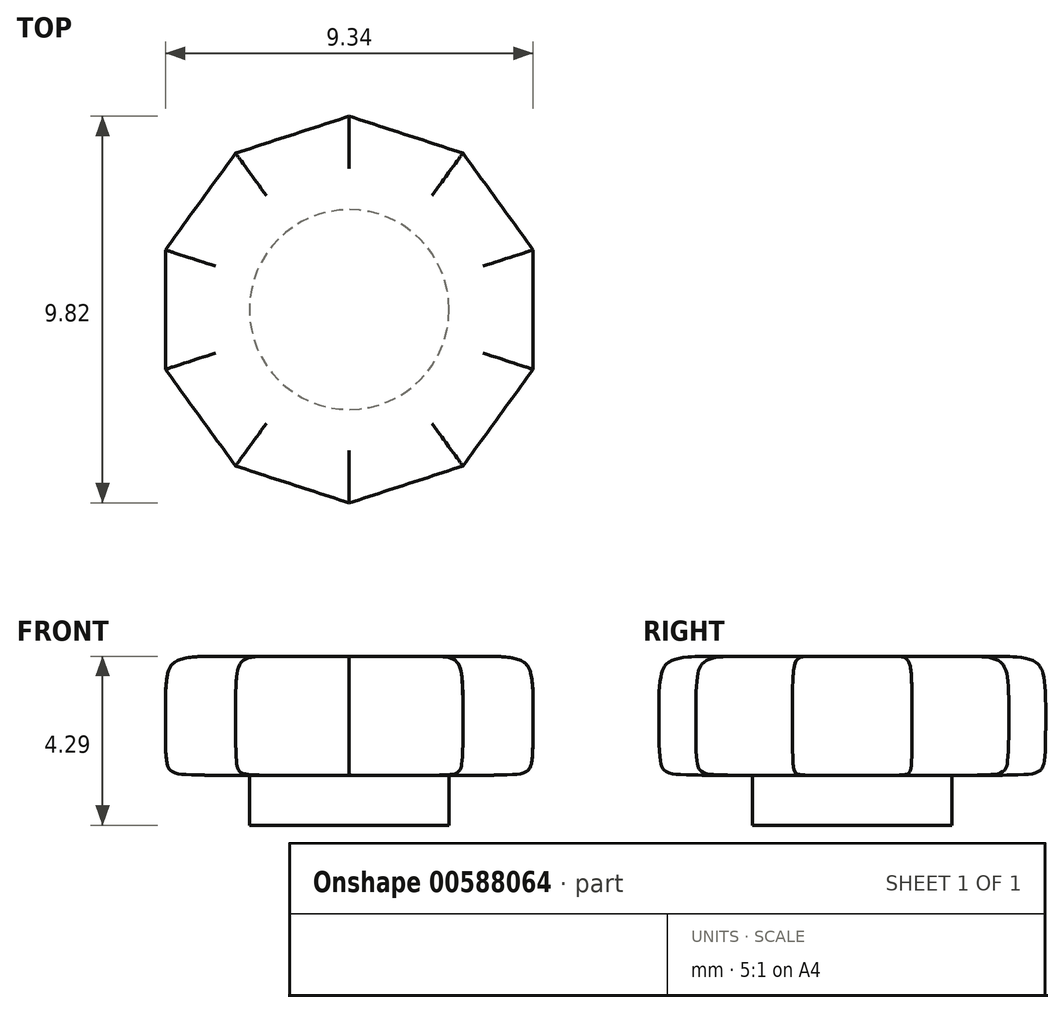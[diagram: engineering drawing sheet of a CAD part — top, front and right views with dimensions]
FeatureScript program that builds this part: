
annotation { "Feature Type Name" : "Feature", "Feature Type Description" : "" }
export const myFeature = defineFeature(function(context is Context, id is Id, definition is map)
    precondition{}
    {
        {
            var Q0;
            Q0=qCreatedBy(makeId("Top.planeOp"),FACE);
            var sketch = newSketch(context, id + "F0", { "sketchPlane" : qUnion([Q0])});
            skCircle(sketch, "E0.cCircle", {"center": v(0, 0) * mm, "radius": 4.67 * mm, "construction": true});
            skLineSegment(sketch, "E0.0", {"start": v(4.67, 1.52) * mm, "end": v(4.67, -1.52) * mm});
            skLineSegment(sketch, "E0.1", {"start": v(4.67, -1.52) * mm, "end": v(2.89, -3.97) * mm});
            skLineSegment(sketch, "E0.2", {"start": v(2.89, -3.97) * mm, "end": v(0, -4.91) * mm});
            skLineSegment(sketch, "E0.3", {"start": v(0, -4.91) * mm, "end": v(-2.89, -3.97) * mm});
            skLineSegment(sketch, "E0.4", {"start": v(-2.89, -3.97) * mm, "end": v(-4.67, -1.52) * mm});
            skLineSegment(sketch, "E0.5", {"start": v(-4.67, -1.52) * mm, "end": v(-4.67, 1.52) * mm});
            skLineSegment(sketch, "E0.6", {"start": v(-4.67, 1.52) * mm, "end": v(-2.89, 3.97) * mm});
            skLineSegment(sketch, "E0.7", {"start": v(-2.89, 3.97) * mm, "end": v(0, 4.91) * mm});
            skLineSegment(sketch, "E0.8", {"start": v(0, 4.91) * mm, "end": v(2.89, 3.97) * mm});
            skLineSegment(sketch, "E0.9", {"start": v(2.89, 3.97) * mm, "end": v(4.67, 1.52) * mm});
            skPoint(sketch, "E0.0.midPoint", {"position": v(4.67, 0) * mm});
            skSolve(sketch);
        }
        {
            var Q0;
            Q0=makeQuery(id+"F0.imprint","IMPRINT",FACE,{"disambiguationData":[TD([[makeQuery(id+"F0.imprint","IMPRINT",EDGE,{"derivedFrom":sQuery(id+"F0.wireOp",EDGE,"E0.0")}),-1.0]])]});
            extrude(context, id + "F1", {"entities" : qUnion([Q0]), "depth" : 3.02 * mm, "offsetDistance" : 25.4 * mm});
        }
        {
            var Q0;
            Q0=qCreatedBy(makeId("Top.planeOp"),FACE);
            var sketch = newSketch(context, id + "F2", { "sketchPlane" : qUnion([Q0])});
            skCircle(sketch, "E1", {"center": v(0, 0) * mm, "radius": 2.54 * mm});
            skSolve(sketch);
        }
        {
            var Q0;
            Q0=makeQuery(id+"F2.imprint","IMPRINT",FACE,{"disambiguationData":[TD([[makeQuery(id+"F2.imprint","IMPRINT",EDGE,{"derivedFrom":sQuery(id+"F2.wireOp",EDGE,"E1")}),1.0]])]});
            extrude(context, id + "F3", {"entities" : qUnion([Q0]), "operationType" : NewBodyOperationType.ADD, "oppositeDirection" : true, "depth" : 1.27 * mm, "offsetDistance" : 25.4 * mm});
        }
        {
            var Q0;
            Q0=makeQuery(id+"F1.opExtrude","CAP_FACE",FACE,{"disambiguationData":[OSD([sQuery(id+"F0.wireOp",EDGE,"E0.0"),sQuery(id+"F0.wireOp",EDGE,"E0.1"),sQuery(id+"F0.wireOp",EDGE,"E0.2"),sQuery(id+"F0.wireOp",EDGE,"E0.3"),sQuery(id+"F0.wireOp",EDGE,"E0.4"),sQuery(id+"F0.wireOp",EDGE,"E0.5"),sQuery(id+"F0.wireOp",EDGE,"E0.6"),sQuery(id+"F0.wireOp",EDGE,"E0.7"),sQuery(id+"F0.wireOp",EDGE,"E0.8"),sQuery(id+"F0.wireOp",EDGE,"E0.9")])],"isStart":false});
            fillet(context, id + "F4", {"entities" : qUnion([Q0]), "radius" : 1.27 * mm, "tangentPropagation" : true, "rho" : .7, "crossSection" : FilletCrossSection.CONIC, "allowEdgeOverflow" : false});
        }
        {
            var Q0;
            Q0=makeQuery(id+"F1.opExtrude","CAP_EDGE",EDGE,{"disambiguationData":[OSD([sQuery(id+"F0.wireOp",EDGE,"E0.3")])],"isStart":true});
            var Q1;
            Q1=makeQuery(id+"F1.opExtrude","CAP_EDGE",EDGE,{"disambiguationData":[OSD([sQuery(id+"F0.wireOp",EDGE,"E0.2")])],"isStart":true});
            var Q2;
            Q2=makeQuery(id+"F1.opExtrude","CAP_EDGE",EDGE,{"disambiguationData":[OSD([sQuery(id+"F0.wireOp",EDGE,"E0.1")])],"isStart":true});
            var Q3;
            Q3=makeQuery(id+"F1.opExtrude","CAP_EDGE",EDGE,{"disambiguationData":[OSD([sQuery(id+"F0.wireOp",EDGE,"E0.0")])],"isStart":true});
            var Q4;
            Q4=makeQuery(id+"F1.opExtrude","CAP_EDGE",EDGE,{"disambiguationData":[OSD([sQuery(id+"F0.wireOp",EDGE,"E0.9")])],"isStart":true});
            var Q5;
            Q5=makeQuery(id+"F1.opExtrude","CAP_EDGE",EDGE,{"disambiguationData":[OSD([sQuery(id+"F0.wireOp",EDGE,"E0.8")])],"isStart":true});
            var Q6;
            Q6=makeQuery(id+"F1.opExtrude","CAP_EDGE",EDGE,{"disambiguationData":[OSD([sQuery(id+"F0.wireOp",EDGE,"E0.7")])],"isStart":true});
            var Q7;
            Q7=makeQuery(id+"F1.opExtrude","CAP_EDGE",EDGE,{"disambiguationData":[OSD([sQuery(id+"F0.wireOp",EDGE,"E0.6")])],"isStart":true});
            var Q8;
            Q8=makeQuery(id+"F1.opExtrude","CAP_EDGE",EDGE,{"disambiguationData":[OSD([sQuery(id+"F0.wireOp",EDGE,"E0.5")])],"isStart":true});
            var Q9;
            Q9=makeQuery(id+"F1.opExtrude","CAP_EDGE",EDGE,{"disambiguationData":[OSD([sQuery(id+"F0.wireOp",EDGE,"E0.4")])],"isStart":true});
            fillet(context, id + "F5", {"entities" : qUnion([Q0, Q1, Q2, Q3, Q4, Q5, Q6, Q7, Q8, Q9]), "radius" : 1.27 * mm, "tangentPropagation" : true, "rho" : .8, "crossSection" : FilletCrossSection.CONIC, "allowEdgeOverflow" : false});
        }
    });
